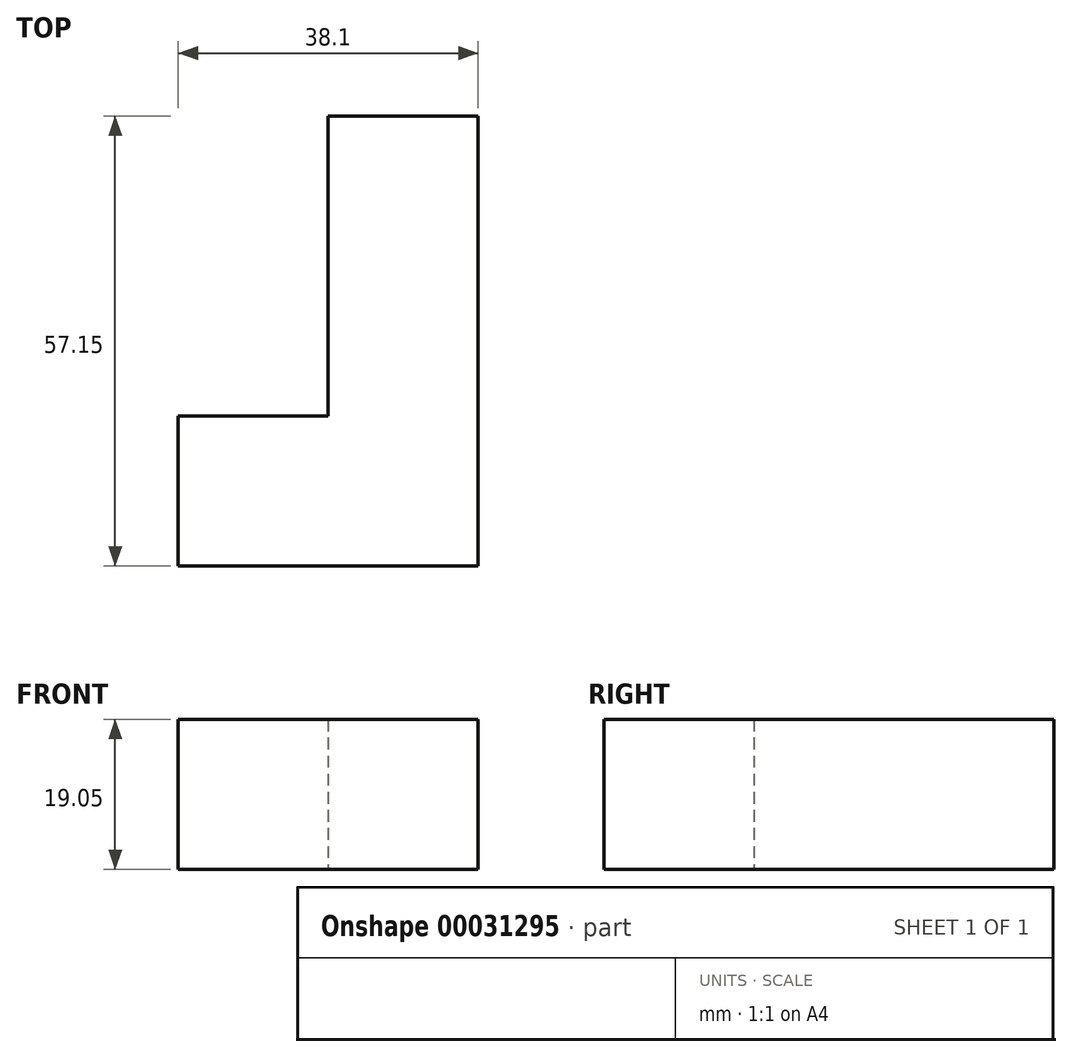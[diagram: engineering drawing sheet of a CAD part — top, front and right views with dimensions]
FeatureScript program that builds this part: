
annotation { "Feature Type Name" : "Feature", "Feature Type Description" : "" }
export const myFeature = defineFeature(function(context is Context, id is Id, definition is map)
    precondition{}
    {
        {
            var Q0;
            Q0=qCreatedBy(makeId("Top.planeOp"),FACE);
            var sketch = newSketch(context, id + "F0", { "sketchPlane" : qUnion([Q0])});
            skLineSegment(sketch, "E0", {"start": v(0, 0) * mm, "end": v(38.1, 0) * mm});
            skLineSegment(sketch, "E1", {"start": v(38.1, 0) * mm, "end": v(38.1, 57.15) * mm});
            skLineSegment(sketch, "E2", {"start": v(19.05, 57.15) * mm, "end": v(19.05, 19.05) * mm});
            skLineSegment(sketch, "E3", {"start": v(19.05, 19.05) * mm, "end": v(0, 19.05) * mm});
            skLineSegment(sketch, "E4", {"start": v(0, 19.05) * mm, "end": v(0, 0) * mm});
            skLineSegment(sketch, "E5", {"start": v(19.05, 57.15) * mm, "end": v(38.1, 57.15) * mm});
            skSolve(sketch);
        }
        {
            var Q0;
            Q0=makeQuery(id+"F0.imprint","IMPRINT",FACE,{"disambiguationData":[TD([[makeQuery(id+"F0.imprint","IMPRINT",EDGE,{"derivedFrom":sQuery(id+"F0.wireOp",EDGE,"E0")}),1.0]])]});
            extrude(context, id + "F1", {"entities" : qUnion([Q0]), "depth" : 19.05 * mm});
        }
    });
